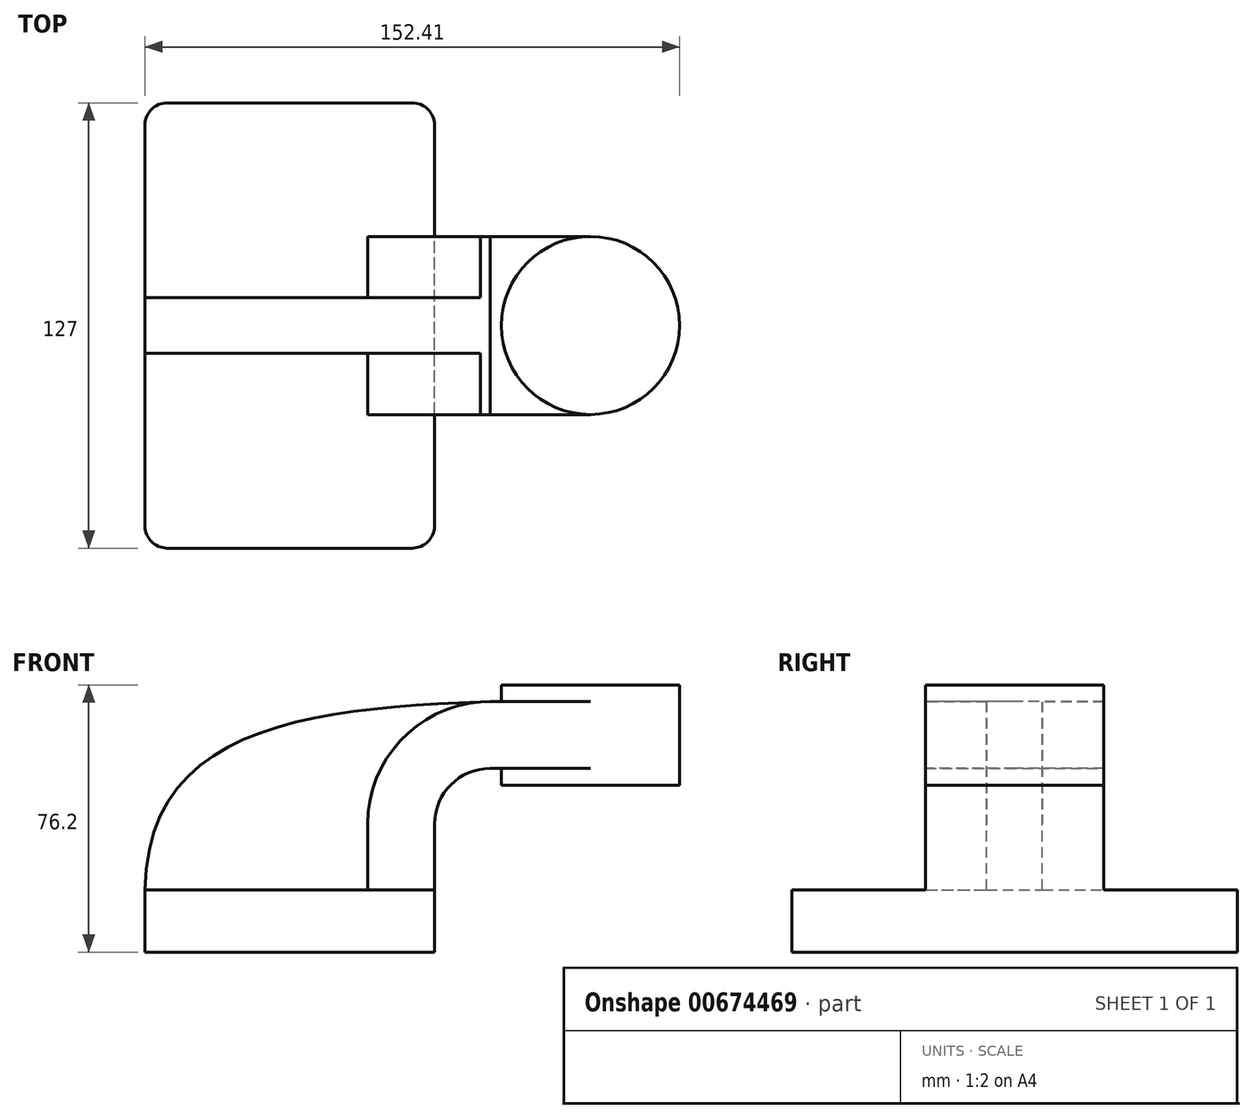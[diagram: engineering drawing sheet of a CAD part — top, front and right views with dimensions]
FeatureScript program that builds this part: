
annotation { "Feature Type Name" : "Feature", "Feature Type Description" : "" }
export const myFeature = defineFeature(function(context is Context, id is Id, definition is map)
    precondition{}
    {
        {
            var Q0;
            Q0=qCreatedBy(makeId("Front.planeOp"),FACE);
            var sketch = newSketch(context, id + "F0", { "sketchPlane" : qUnion([Q0])});
            skLineSegment(sketch, "E0.bottom", {"start": v(41.28, -8.89) * mm, "end": v(-41.28, -8.9) * mm});
            skLineSegment(sketch, "E0.top", {"start": v(41.27, 8.9) * mm, "end": v(-41.28, 8.9) * mm});
            skLineSegment(sketch, "E0.left", {"start": v(41.28, -8.89) * mm, "end": v(41.28, 8.9) * mm});
            skLineSegment(sketch, "E0.right", {"start": v(-41.28, -8.89) * mm, "end": v(-41.28, 8.9) * mm});
            skPoint(sketch, "E0.middle", {"position": v(0, 0) * mm});
            skLineSegment(sketch, "E1.bottom", {"start": v(60.32, 38.74) * mm, "end": v(111.12, 38.74) * mm});
            skLineSegment(sketch, "E1.top", {"start": v(60.32, 67.31) * mm, "end": v(111.12, 67.31) * mm});
            skLineSegment(sketch, "E1.left", {"start": v(60.32, 38.74) * mm, "end": v(60.32, 67.31) * mm});
            skLineSegment(sketch, "E1.right", {"start": v(111.12, 38.74) * mm, "end": v(111.12, 67.31) * mm});
            skPoint(sketch, "E1.middle", {"position": v(85.72, 53.02) * mm});
            skLineSegment(sketch, "E2", {"start": v(41.27, 8.9) * mm, "end": v(41.27, 27.64) * mm});
            skArc(sketch, "E3", {"start": v(41.27, 27.64) * mm, "mid": v(45.92, 38.86) * mm, "end": v(57.15, 43.51) * mm});
            skLineSegment(sketch, "E4", {"start": v(57.15, 43.51) * mm, "end": v(85.72, 43.51) * mm});
            skPoint(sketch, "E5", {"position": v(85.72, 38.74) * mm});
            skLineSegment(sketch, "E6.0", {"start": v(57.15, 62.56) * mm, "end": v(85.72, 62.56) * mm});
            skArc(sketch, "E6.1", {"start": v(22.23, 27.64) * mm, "mid": v(32.45, 52.33) * mm, "end": v(57.15, 62.56) * mm});
            skLineSegment(sketch, "E6.2", {"start": v(22.22, 8.9) * mm, "end": v(22.22, 27.64) * mm});
            skLineSegment(sketch, "E7", {"start": v(85.72, 38.74) * mm, "end": v(85.72, 67.31) * mm});
            skFitSpline(sketch, "E8", {"points": [v(-41.28, 8.89) * mm, v(57.15, 62.56) * mm], "startDerivative": vector(1.9, 144.75) * mm, "endDerivative": vector(143.87, 5.63) * mm});
            skSolve(sketch);
        }
        {
            var Q0;
            Q0=makeQuery(id+"F0.imprint","IMPRINT",FACE,{"disambiguationData":[TD([[makeQuery(id+"F0.imprint","IMPRINT",EDGE,{"derivedFrom":sQuery(id+"F0.wireOp",EDGE,"E0.bottom")}),-1.0]])]});
            extrude(context, id + "F1", {"entities" : qUnion([Q0]), "endBound" : BoundingType.SYMMETRIC, "depth" : 127 * mm, "offsetDistance" : 25.4 * mm});
        }
        {
            var Q0;
            {var subQ1=sQuery(id+"F0.wireOp",EDGE,"E2");Q0=makeQuery(id+"F0.imprint","IMPRINT",FACE,{"disambiguationData":[TD([[makeQuery(id+"F0.imprint","IMPRINT",EDGE,{"derivedFrom":subQ1}),1.0]])]});}
            var Q1;
            {var subQ0=sQuery(id+"F0.wireOp",EDGE,"E4");var subQ1=sQuery(id+"F0.wireOp",EDGE,"E1.left");var subQ2=makeQuery(id+"F0.imprint","INTERSECT",VERTEX,{"derivedFrom":[subQ1,subQ0]});Q1=makeQuery(id+"F0.imprint","IMPRINT",FACE,{"disambiguationData":[TD([[makeQuery(id+"F0.imprint","IMPRINT",EDGE,{"disambiguationData":[TD([[subQ2,-1.0]])],"derivedFrom":subQ1}),-1.0]])]});}
            extrude(context, id + "F2", {"entities" : qUnion([Q0, Q1]), "operationType" : NewBodyOperationType.ADD, "endBound" : BoundingType.SYMMETRIC, "depth" : 50.8 * mm, "offsetDistance" : 25.4 * mm});
        }
        {
            var Q0;
            {var subQ3=sQuery(id+"F0.wireOp",EDGE,"E6.2");Q0=makeQuery(id+"F0.imprint","IMPRINT",FACE,{"disambiguationData":[TD([[makeQuery(id+"F0.imprint","IMPRINT",EDGE,{"derivedFrom":subQ3}),1.0]])]});}
            extrude(context, id + "F3", {"entities" : qUnion([Q0]), "operationType" : NewBodyOperationType.ADD, "endBound" : BoundingType.SYMMETRIC, "depth" : 15.88 * mm, "offsetDistance" : 25.4 * mm});
        }
        {
            var Q0;
            {var subQ4=sQuery(id+"F0.wireOp",EDGE,"E1.right");Q0=makeQuery(id+"F0.imprint","IMPRINT",FACE,{"disambiguationData":[TD([[makeQuery(id+"F0.imprint","IMPRINT",EDGE,{"derivedFrom":subQ4}),1.0]])]});}
            var Q1;
            Q1=sQuery(id+"F0.wireOp",EDGE,"E7");
            revolve(context, id + "F4", {"operationType" : NewBodyOperationType.ADD, "entities" : qUnion([Q0]), "axis" : qUnion([Q1]), "revolveType" : RevolveType.FULL});
        }
        {
            var Q0;
            Q0=makeQuery(id+"F1.opExtrude","CAP_EDGE",EDGE,{"disambiguationData":[OSD([sQuery(id+"F0.wireOp",EDGE,"E0.right")])],"isStart":false});
            var Q1;
            Q1=makeQuery(id+"F1.opExtrude","CAP_EDGE",EDGE,{"disambiguationData":[OSD([sQuery(id+"F0.wireOp",EDGE,"E0.left")])],"isStart":false});
            var Q2;
            Q2=makeQuery(id+"F1.opExtrude","CAP_EDGE",EDGE,{"disambiguationData":[OSD([sQuery(id+"F0.wireOp",EDGE,"E0.left")])],"isStart":true});
            var Q3;
            Q3=makeQuery(id+"F1.opExtrude","CAP_EDGE",EDGE,{"disambiguationData":[OSD([sQuery(id+"F0.wireOp",EDGE,"E0.right")])],"isStart":true});
            fillet(context, id + "F5", {"entities" : qUnion([Q0, Q1, Q2, Q3]), "radius" : 6.35 * mm, "tangentPropagation" : true, "allowEdgeOverflow" : false});
        }
    });
